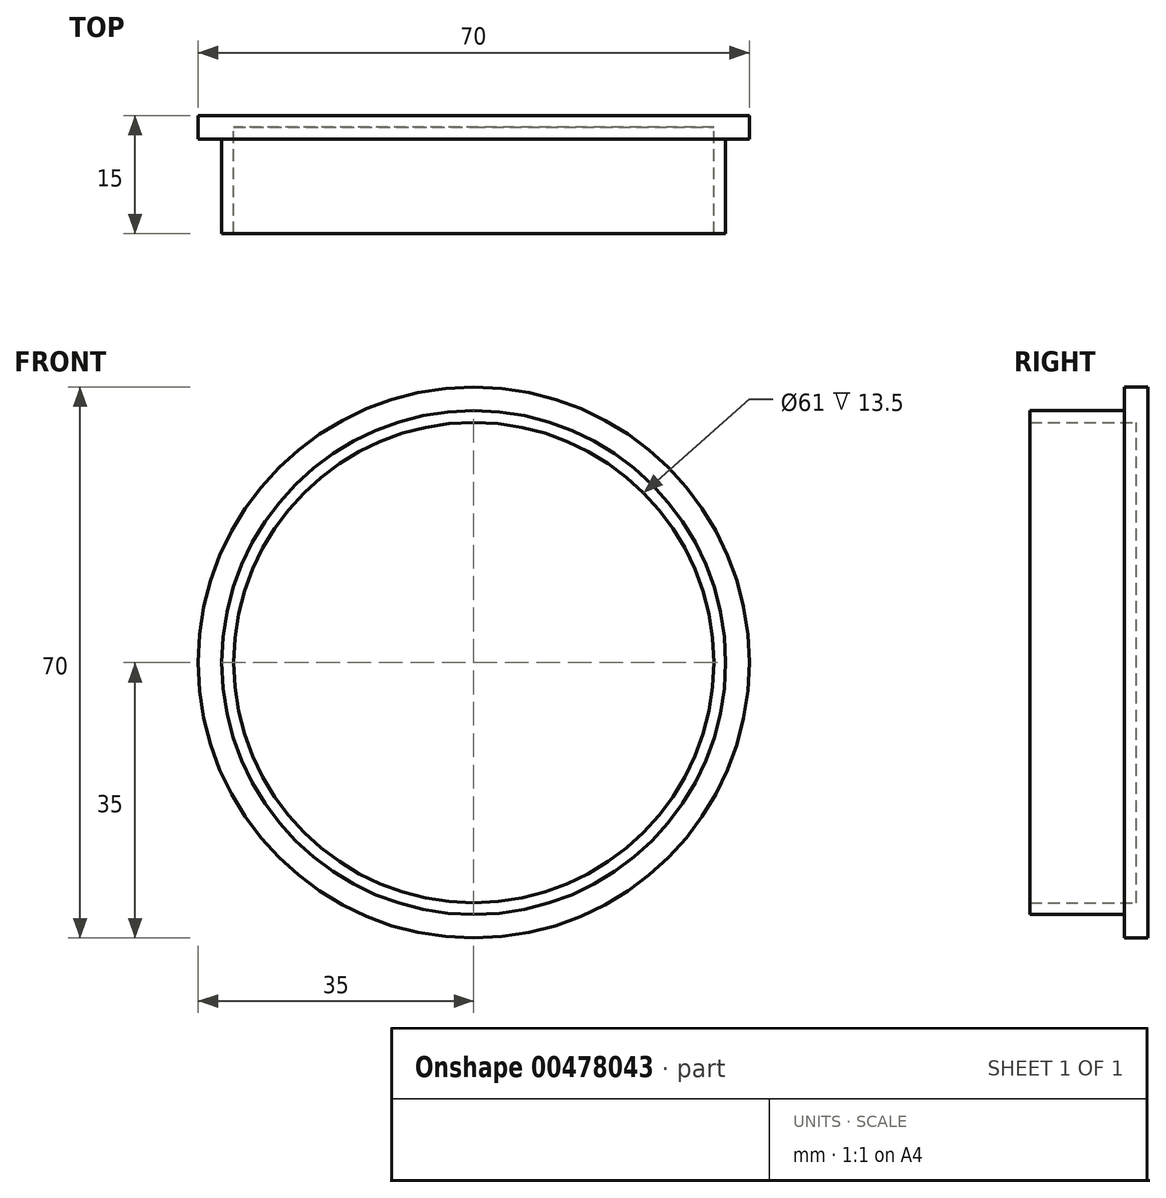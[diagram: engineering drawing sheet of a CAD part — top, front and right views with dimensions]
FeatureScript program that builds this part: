
annotation { "Feature Type Name" : "Feature", "Feature Type Description" : "" }
export const myFeature = defineFeature(function(context is Context, id is Id, definition is map)
    precondition{}
    {
        {
            var Q0;
            Q0=qCreatedBy(makeId("Front.planeOp"),FACE);
            var sketch = newSketch(context, id + "F0", { "sketchPlane" : qUnion([Q0]), "disableImprinting" : false});
            skCircle(sketch, "E0", {"center": v(0, 0) * mm, "radius": 35 * mm});
            skSolve(sketch);
        }
        {
            var Q0;
            Q0 = qSketchRegion(id + "F0", true);
            extrude(context, id + "F1", {"entities" : qUnion([Q0]), "flatOperationType" : FlatOperationType.REMOVE, "offsetDistance" : 25 * mm, "startOffsetBound" : StartOffsetType.BLIND, "startOffsetDistance" : 25 * mm, "depth" : 3 * mm, "domain" : OperationDomain.MODEL});
        }
        {
            var Q0;
            Q0=qCreatedBy(makeId("Front.planeOp"),FACE);
            var sketch = newSketch(context, id + "F2", { "sketchPlane" : qUnion([Q0]), "disableImprinting" : false});
            skCircle(sketch, "E1", {"center": v(0, 0) * mm, "radius": 32 * mm});
            skSolve(sketch);
        }
        {
            var Q0;
            Q0 = qSketchRegion(id + "F2", true);
            extrude(context, id + "F3", {"entities" : qUnion([Q0]), "operationType" : NewBodyOperationType.ADD, "depth" : 15 * mm});
        }
        {
            var Q0;
            Q0=makeQuery(id+"F3.opExtrude","CAP_FACE",FACE,{"disambiguationData":[OSD([sQuery(id+"F2.wireOp",EDGE,"E1")])],"isStart":false});
            shell(context, id + "F4", {"entities" : qUnion([Q0]), "thickness" : 1.5 * mm});
        }
    });
